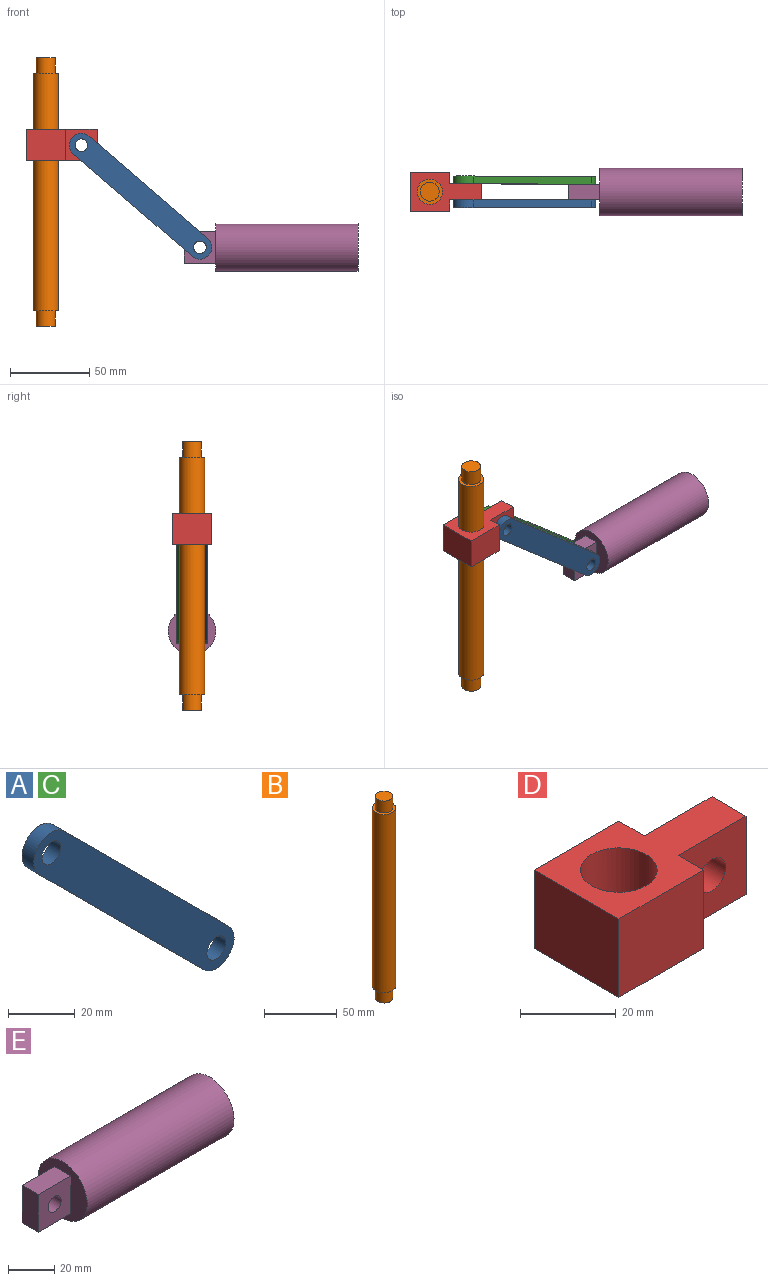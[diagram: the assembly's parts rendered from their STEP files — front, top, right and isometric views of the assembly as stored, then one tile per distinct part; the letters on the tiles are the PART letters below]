
ASSEMBLY  parts=5 mates=6
PART A: 8 faces, bbox 85x5x85 mm
  f0: plane 70x70mm, normal (-0.71,0,-0.71), area 495mm2, adj f1,f4,f6,f7
  f1: cylinder r=7.5mm len=12.8mm, axis (0,1,0), area 117.8mm2, adj f0,f2,f6,f7
  f2: plane 70x70mm, normal (0.71,0,0.71), area 495mm2, adj f1,f4,f6,f7
  f3: cylinder r=4mm len=8mm, axis (0,1,0), area 125.7mm2, adj f6,f7
  f4: cylinder r=7.5mm len=12.8mm, axis (0,1,0), area 117.8mm2, adj f0,f2,f6,f7
  f5: cylinder r=4mm len=8mm, axis (0,1,0), area 125.7mm2, adj f6,f7
  f6: plane 85x85mm, normal (0,-1,0), area 1561.1mm2, adj f0,f1,f2,f3,f4,f5
  f7: plane 85x85mm, normal (0,1,0), area 1561.1mm2, adj f0,f1,f2,f3,f4,f5
PART B: 7 faces, bbox 16x16x170 mm
  f0: plane 12x12mm, normal (0,0,1), area 113.1mm2, adj f1
  f1: cylinder r=6mm len=12mm, axis (0,0,1), area 377mm2, adj f0,f2
  f2: plane 16x16mm, normal (0,0,1), area 88mm2, adj f1,f3
  f3: cylinder r=8mm len=150mm, axis (0,0,1), area 7539.8mm2, adj f2,f4
  f4: plane 16x16mm, normal (0,0,-1), area 88mm2, adj f3,f5
  f5: cylinder r=6mm len=12mm, axis (0,0,1), area 377mm2, adj f4,f6
  f6: plane 12x12mm, normal (0,0,-1), area 113.1mm2, adj f5
PART C: same geometry as A
PART D: 12 faces, bbox 45x25x20 mm
  f0: plane 20x7.5mm, normal (1,0,0), area 150mm2, adj f1,f3,f6,f10
  f1: plane 45x25mm, normal (0,0,1), area 623.9mm2, adj f0,f2,f4,f5,f6,f8,f9,f10
  f2: plane 25x20mm, normal (-1,0,0), area 500mm2, adj f1,f3,f5,f6
  f3: plane 45x25mm, normal (0,0,-1), area 623.9mm2, adj f0,f2,f4,f5,f6,f8,f9,f10
  f4: plane 20x7.5mm, normal (1,0,0), area 150mm2, adj f1,f3,f5,f9
  f5: plane 25x20mm, normal (0,-1,0), area 500mm2, adj f1,f2,f3,f4
  f6: plane 25x20mm, normal (0,1,0), area 500mm2, adj f0,f1,f2,f3
  f7: cylinder r=4mm len=10mm, axis (0,1,0), area 251.3mm2, adj f9,f10
  f8: plane 20x10mm, normal (1,0,0), area 200mm2, adj f1,f3,f9,f10
  f9: plane 20x20mm, normal (0,-1,0), area 349.7mm2, adj f1,f3,f4,f7,f8
  f10: plane 20x20mm, normal (0,1,0), area 349.7mm2, adj f0,f1,f3,f7,f8
  f11: cylinder r=8mm len=20mm, axis (0,0,1), area 1005.3mm2, adj f1,f3
PART E: 9 faces, bbox 110x30x30 mm
  f0: plane 30x30mm, normal (-1,0,0), area 506.9mm2, adj f2,f3,f6,f7,f8
  f1: plane 30x30mm, normal (1,0,0), area 706.9mm2, adj f2
  f2: cylinder r=15mm len=90mm, axis (1,0,0), area 8482.3mm2, adj f0,f1
  f3: plane 20x10mm, normal (0,0,1), area 200mm2, adj f0,f4,f7,f8
  f4: plane 20x10mm, normal (-1,0,0), area 200mm2, adj f3,f6,f7,f8
  f5: cylinder r=4mm len=10mm, axis (0,1,0), area 251.3mm2, adj f7,f8
  f6: plane 20x10mm, normal (0,0,-1), area 200mm2, adj f0,f4,f7,f8
  f7: plane 20x20mm, normal (0,-1,0), area 349.7mm2, adj f0,f3,f4,f5,f6
  f8: plane 20x20mm, normal (0,1,0), area 349.7mm2, adj f0,f3,f4,f5,f6
PLACE A rot(axis=(0,-1,0),4.3deg) t=(7.39,-5.17,13.22)mm
PLACE B t=(-0.09,-5.17,0)mm fixed
PLACE C rot(axis=(0,-1,0),4.3deg) t=(7.39,9.83,13.22)mm
PLACE D t=(-0.09,-5.17,14.61)mm
PLACE E t=(4.91,-5.17,20)mm
MATE revolute A.f3 <-> D.f7  axis (0,1,0) through (22.41,-10.17,114.61)mm
MATE planar E.f6 <-> B.f1  axis (0,0,-1) through (97.41,-5.17,40)mm
MATE revolute C.f3 <-> D.f7  axis (0,-1,0) through (22.41,-0.17,114.61)mm
MATE revolute E.f5 <-> A.f1  axis (0,-1,0) through (97.41,-10.17,50)mm
MATE cylindrical A.f1 <-> C.f1  axis (0,-1,0) through (97.41,-15.17,50)mm
MATE slider D.f11 <-> B.f1  axis (0,0,1) through (-0.09,-5.17,124.61)mm
